# Revit family: FU_Inspec_Archal_XL_5-1
name_source: partatom
category: Furniture
units: mm (PartAtom-declared; Revit-internal decimal feet)

## family parameters
Always vertical = Yes
Cut with Voids When Loaded = No
OmniClass Number = 23.40.20.00
OmniClass Title = General Furniture and Specialties
Room Calculation Point = No
Shared = No
Work Plane-Based = No

## types (2) — shared parameters
Assembly Code = E2020
Castor Material = Metal - Chrome - Polished
Keynote = 46.B
Manufacturer = Inspec
URL = https://inspecfurniture.com
zero-valued in all types: Default Elevation, Depth, Height, Thickness, Width

## per-type parameters (varying)
| type | Armrest | Armrest Material | Description | Frame Material | Seat Material |
| archal xl 5.1 | No | Metal - Graphite - Matte | Conference chair on a 360° swivel powder coated or polished aluminum base on casters. Fully upholstered with quilting detail. | Metal - Graphite - Matte | Fabric - Graphite Grey Woven |
| archal xl 5.2 | Yes | Metall - Aluminium - Blank | Conference armchair on a 360° swivel powder coated or polished aluminum base on casters. Fully upholstered with quilting detail. | Metall - Aluminium - Blank | Leather - Rustical - Brown |

note: column(s) folded — value = type name in every type: Model

## geometry (parser evidence)
native form markers: Blend x3, Sweep x2
no freeform markers — native parametric forms only
